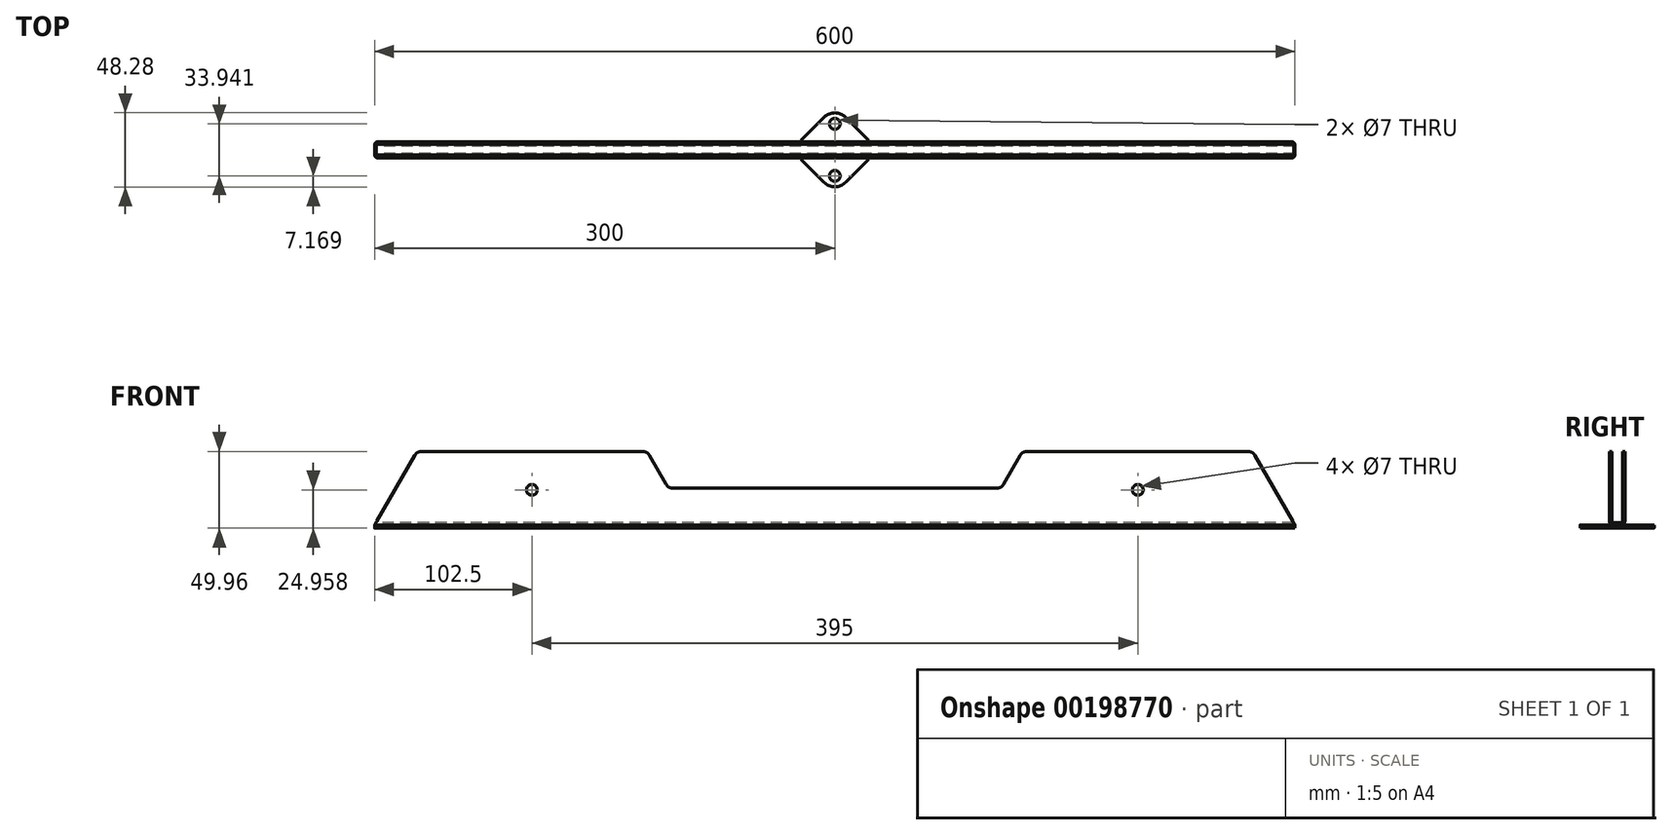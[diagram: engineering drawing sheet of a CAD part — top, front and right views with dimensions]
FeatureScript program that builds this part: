
annotation { "Feature Type Name" : "Feature", "Feature Type Description" : "" }
export const myFeature = defineFeature(function(context is Context, id is Id, definition is map)
    precondition{}
    {
        {
            var Q0;
            Q0=qCreatedBy(makeId("Top.planeOp"),FACE);
            var sketch = newSketch(context, id + "F0", { "sketchPlane" : qUnion([Q0])});
            skLineSegment(sketch, "E0.bottom", {"start": v(-21.21, 7.07) * mm, "end": v(-7.07, 21.21) * mm});
            skLineSegment(sketch, "E0.top", {"start": v(7.07, -21.21) * mm, "end": v(21.21, -7.07) * mm});
            skLineSegment(sketch, "E0.left", {"start": v(-21.21, -7.07) * mm, "end": v(-7.07, -21.21) * mm});
            skLineSegment(sketch, "E0.right", {"start": v(7.07, 21.21) * mm, "end": v(21.21, 7.07) * mm});
            skPoint(sketch, "E0.middle", {"position": v(0, 0) * mm});
            skPoint(sketch, "E1.visualSharp", {"position": v(-28.28, 0) * mm});
            skArc(sketch, "E1.filletArc", {"start": v(-21.21, 7.07) * mm, "mid": v(-24.14, 0) * mm, "end": v(-21.21, -7.07) * mm});
            skPoint(sketch, "E2.visualSharp", {"position": v(0, 28.28) * mm});
            skArc(sketch, "E2.filletArc", {"start": v(7.07, 21.21) * mm, "mid": v(0, 24.14) * mm, "end": v(-7.07, 21.21) * mm});
            skPoint(sketch, "E3.visualSharp", {"position": v(28.28, 0) * mm});
            skArc(sketch, "E3.filletArc", {"start": v(21.21, -7.07) * mm, "mid": v(24.14, 0) * mm, "end": v(21.21, 7.07) * mm});
            skPoint(sketch, "E4.visualSharp", {"position": v(0, -28.28) * mm});
            skArc(sketch, "E4.filletArc", {"start": v(-7.07, -21.21) * mm, "mid": v(0, -24.14) * mm, "end": v(7.07, -21.21) * mm});
            skLineSegment(sketch, "E5.bottom", {"start": v(0, 16.97) * mm, "end": v(-16.97, 0) * mm, "construction": true});
            skLineSegment(sketch, "E5.top", {"start": v(16.97, 0) * mm, "end": v(0, -16.97) * mm, "construction": true});
            skLineSegment(sketch, "E5.left", {"start": v(0, 16.97) * mm, "end": v(16.97, 0) * mm, "construction": true});
            skLineSegment(sketch, "E5.right", {"start": v(-16.97, 0) * mm, "end": v(0, -16.97) * mm, "construction": true});
            skCircle(sketch, "E6", {"center": v(0, 16.97) * mm, "radius": 3.5 * mm});
            skCircle(sketch, "E7", {"center": v(16.97, 0) * mm, "radius": 3.5 * mm});
            skCircle(sketch, "E8", {"center": v(0, -16.97) * mm, "radius": 3.5 * mm});
            skCircle(sketch, "E9", {"center": v(-16.97, 0) * mm, "radius": 3.5 * mm});
            skSolve(sketch);
        }
        {
            var Q0;
            Q0 = qSketchRegion(id + "F0", true);
            extrude(context, id + "F1", {"entities" : qUnion([Q0]), "depth" : 2 * mm});
        }
        {
            var Q0;
            Q0=qCreatedBy(makeId("Front.planeOp"),FACE);
            var sketch = newSketch(context, id + "F2", { "sketchPlane" : qUnion([Q0])});
            skLineSegment(sketch, "E10", {"start": v(0, 2) * mm, "end": v(0, 49.96) * mm, "construction": true});
            skLineSegment(sketch, "E11.bottom", {"start": v(300, 49.96) * mm, "end": v(-300, 49.96) * mm, "construction": true});
            skLineSegment(sketch, "E11.top", {"start": v(300, 2) * mm, "end": v(-300, 2) * mm});
            skLineSegment(sketch, "E11.left", {"start": v(300, 49.96) * mm, "end": v(300, 2) * mm, "construction": true});
            skLineSegment(sketch, "E11.right", {"start": v(-300, 49.96) * mm, "end": v(-300, 2) * mm, "construction": true});
            skPoint(sketch, "E11.middle", {"position": v(0, 25.98) * mm});
            skLineSegment(sketch, "E12", {"start": v(-300, 2) * mm, "end": v(-272.31, 49.96) * mm});
            skLineSegment(sketch, "E13", {"start": v(-272.31, 49.96) * mm, "end": v(-122.31, 49.96) * mm});
            skLineSegment(sketch, "E14", {"start": v(-122.31, 49.96) * mm, "end": v(-108.47, 25.98) * mm});
            skLineSegment(sketch, "E15", {"start": v(-108.47, 25.98) * mm, "end": v(0, 25.98) * mm});
            skLineSegment(sketch, "E16.MirrorCS", {"start": v(122.31, 49.96) * mm, "end": v(108.47, 25.98) * mm});
            skLineSegment(sketch, "E17.MirrorCS", {"start": v(108.47, 25.98) * mm, "end": v(0, 25.98) * mm});
            skLineSegment(sketch, "E18.MirrorCS", {"start": v(272.31, 49.96) * mm, "end": v(122.31, 49.96) * mm});
            skLineSegment(sketch, "E19.MirrorCS", {"start": v(300, 2) * mm, "end": v(272.31, 49.96) * mm});
            skSolve(sketch);
        }
        {
            var Q0;
            Q0 = qSketchRegion(id + "F2", true);
            extrude(context, id + "F3", {"entities" : qUnion([Q0]), "depth" : 10.2 * mm, "symmetric" : true});
        }
        {
            var Q0;
            Q0=makeQuery(id+"F3.opExtrude","CAP_EDGE",EDGE,{"disambiguationData":[OSD([sQuery(id+"F2.wireOp",EDGE,"E11.top")])],"isStart":false});
            var Q1;
            Q1=makeQuery(id+"F3.opExtrude","CAP_EDGE",EDGE,{"disambiguationData":[OSD([sQuery(id+"F2.wireOp",EDGE,"E11.top")])],"isStart":true});
            fillet(context, id + "F4", {"entities" : qUnion([Q0, Q1]), "radius" : 2.6 * mm, "tangentPropagation" : true, "allowEdgeOverflow" : false});
        }
        {
            var Q0;
            Q0=makeQuery(id+"F3.opExtrude","SWEPT_EDGE",EDGE,{"disambiguationData":[OSD([sQuery(id+"F2.wireOp",EDGE,"E12"),sQuery(id+"F2.wireOp",EDGE,"E13")])]});
            var Q1;
            Q1=makeQuery(id+"F3.opExtrude","SWEPT_EDGE",EDGE,{"disambiguationData":[OSD([sQuery(id+"F2.wireOp",EDGE,"E13"),sQuery(id+"F2.wireOp",EDGE,"E14")])]});
            var Q2;
            Q2=makeQuery(id+"F3.opExtrude","SWEPT_EDGE",EDGE,{"disambiguationData":[OSD([sQuery(id+"F2.wireOp",EDGE,"E14"),sQuery(id+"F2.wireOp",EDGE,"E15")])]});
            var Q3;
            Q3=makeQuery(id+"F3.opExtrude","SWEPT_EDGE",EDGE,{"disambiguationData":[OSD([sQuery(id+"F2.wireOp",EDGE,"E16.MirrorCS"),sQuery(id+"F2.wireOp",EDGE,"E18.MirrorCS")])]});
            var Q4;
            Q4=makeQuery(id+"F3.opExtrude","SWEPT_EDGE",EDGE,{"disambiguationData":[OSD([sQuery(id+"F2.wireOp",EDGE,"E16.MirrorCS"),sQuery(id+"F2.wireOp",EDGE,"E17.MirrorCS")])]});
            var Q5;
            Q5=makeQuery(id+"F3.opExtrude","SWEPT_EDGE",EDGE,{"disambiguationData":[OSD([sQuery(id+"F2.wireOp",EDGE,"E18.MirrorCS"),sQuery(id+"F2.wireOp",EDGE,"E19.MirrorCS")])]});
            fillet(context, id + "F5", {"entities" : qUnion([Q0, Q1, Q2, Q3, Q4, Q5]), "radius" : 5 * mm, "tangentPropagation" : true, "allowEdgeOverflow" : false});
        }
        {
            var Q0;
            Q0=makeQuery(id+"F3.opExtrude","SWEPT_FACE",FACE,{"disambiguationData":[OSD([sQuery(id+"F2.wireOp",EDGE,"E12")])]});
            var Q1;
            Q1=makeQuery(id+"F5.opFillet","BLEND_FACE",FACE,{"disambiguationData":[OSD([sQuery(id+"F2.wireOp",EDGE,"E12"),sQuery(id+"F2.wireOp",EDGE,"E13")])]});
            var Q2;
            Q2=makeQuery(id+"F3.opExtrude","SWEPT_FACE",FACE,{"disambiguationData":[OSD([sQuery(id+"F2.wireOp",EDGE,"E13")])]});
            var Q3;
            Q3=makeQuery(id+"F3.opExtrude","SWEPT_FACE",FACE,{"disambiguationData":[OSD([sQuery(id+"F2.wireOp",EDGE,"E15"),sQuery(id+"F2.wireOp",EDGE,"E17.MirrorCS")])]});
            var Q4;
            Q4=makeQuery(id+"F5.opFillet","BLEND_FACE",FACE,{"disambiguationData":[OSD([sQuery(id+"F2.wireOp",EDGE,"E14"),sQuery(id+"F2.wireOp",EDGE,"E15")])]});
            var Q5;
            Q5=makeQuery(id+"F3.opExtrude","SWEPT_FACE",FACE,{"disambiguationData":[OSD([sQuery(id+"F2.wireOp",EDGE,"E14")])]});
            var Q6;
            Q6=makeQuery(id+"F5.opFillet","BLEND_FACE",FACE,{"disambiguationData":[OSD([sQuery(id+"F2.wireOp",EDGE,"E13"),sQuery(id+"F2.wireOp",EDGE,"E14")])]});
            var Q7;
            Q7=makeQuery(id+"F5.opFillet","BLEND_FACE",FACE,{"disambiguationData":[OSD([sQuery(id+"F2.wireOp",EDGE,"E16.MirrorCS"),sQuery(id+"F2.wireOp",EDGE,"E17.MirrorCS")])]});
            var Q8;
            Q8=makeQuery(id+"F3.opExtrude","SWEPT_FACE",FACE,{"disambiguationData":[OSD([sQuery(id+"F2.wireOp",EDGE,"E16.MirrorCS")])]});
            var Q9;
            Q9=makeQuery(id+"F5.opFillet","BLEND_FACE",FACE,{"disambiguationData":[OSD([sQuery(id+"F2.wireOp",EDGE,"E16.MirrorCS"),sQuery(id+"F2.wireOp",EDGE,"E18.MirrorCS")])]});
            var Q10;
            Q10=makeQuery(id+"F3.opExtrude","SWEPT_FACE",FACE,{"disambiguationData":[OSD([sQuery(id+"F2.wireOp",EDGE,"E18.MirrorCS")])]});
            var Q11;
            Q11=makeQuery(id+"F5.opFillet","BLEND_FACE",FACE,{"disambiguationData":[OSD([sQuery(id+"F2.wireOp",EDGE,"E18.MirrorCS"),sQuery(id+"F2.wireOp",EDGE,"E19.MirrorCS")])]});
            var Q12;
            Q12=makeQuery(id+"F3.opExtrude","SWEPT_FACE",FACE,{"disambiguationData":[OSD([sQuery(id+"F2.wireOp",EDGE,"E19.MirrorCS")])]});
            shell(context, id + "F6", {"entities" : qUnion([Q0, Q1, Q2, Q3, Q4, Q5, Q6, Q7, Q8, Q9, Q10, Q11, Q12]), "thickness" : 1.6 * mm});
        }
        {
            var Q0;
            Q0=makeQuery(id+"F1.opExtrude","CAP_FACE",FACE,{"disambiguationData":[OSD([sQuery(id+"F0.wireOp",EDGE,"E0.bottom"),sQuery(id+"F0.wireOp",EDGE,"E0.top"),sQuery(id+"F0.wireOp",EDGE,"E0.left"),sQuery(id+"F0.wireOp",EDGE,"E0.right"),sQuery(id+"F0.wireOp",EDGE,"E1.filletArc"),sQuery(id+"F0.wireOp",EDGE,"E2.filletArc"),sQuery(id+"F0.wireOp",EDGE,"E3.filletArc"),sQuery(id+"F0.wireOp",EDGE,"E4.filletArc"),sQuery(id+"F0.wireOp",EDGE,"E6"),sQuery(id+"F0.wireOp",EDGE,"E7"),sQuery(id+"F0.wireOp",EDGE,"E8"),sQuery(id+"F0.wireOp",EDGE,"E9")])],"isStart":true});
            var sketch = newSketch(context, id + "F7", { "sketchPlane" : qUnion([Q0])});
            skLineSegment(sketch, "E20", {"start": v(-14.14, -14.14) * mm, "end": v(14.14, 14.14) * mm, "construction": true});
            skLineSegment(sketch, "E21.bottom", {"start": v(298, -5.1) * mm, "end": v(-298, -5.1) * mm});
            skLineSegment(sketch, "E21.top", {"start": v(298, 5.1) * mm, "end": v(-298, 5.1) * mm});
            skLineSegment(sketch, "E21.left", {"start": v(300, -3.1) * mm, "end": v(300, 3.1) * mm});
            skLineSegment(sketch, "E21.right", {"start": v(-300, -3.1) * mm, "end": v(-300, 3.1) * mm});
            skPoint(sketch, "E21.middle", {"position": v(0, 0) * mm});
            skPoint(sketch, "E22.visualSharp", {"position": v(300, -5.1) * mm});
            skArc(sketch, "E22.filletArc", {"start": v(298, -5.1) * mm, "mid": v(299.41, -4.51) * mm, "end": v(300, -3.1) * mm});
            skPoint(sketch, "E23.visualSharp", {"position": v(-300, -5.1) * mm});
            skArc(sketch, "E23.filletArc", {"start": v(-300, -3.1) * mm, "mid": v(-299.41, -4.51) * mm, "end": v(-298, -5.1) * mm});
            skPoint(sketch, "E24.visualSharp", {"position": v(300, 5.1) * mm});
            skArc(sketch, "E24.filletArc", {"start": v(300, 3.1) * mm, "mid": v(299.41, 4.51) * mm, "end": v(298, 5.1) * mm});
            skPoint(sketch, "E25.visualSharp", {"position": v(-300, 5.1) * mm});
            skArc(sketch, "E25.filletArc", {"start": v(-298, 5.1) * mm, "mid": v(-299.41, 4.51) * mm, "end": v(-300, 3.1) * mm});
            skSolve(sketch);
        }
        {
            var Q0;
            Q0 = qSketchRegion(id + "F7", true);
            var Q1;
            Q1=makeQuery(id+"F1.opExtrude","CAP_FACE",FACE,{"disambiguationData":[OSD([sQuery(id+"F0.wireOp",EDGE,"E0.bottom"),sQuery(id+"F0.wireOp",EDGE,"E0.top"),sQuery(id+"F0.wireOp",EDGE,"E0.left"),sQuery(id+"F0.wireOp",EDGE,"E0.right"),sQuery(id+"F0.wireOp",EDGE,"E1.filletArc"),sQuery(id+"F0.wireOp",EDGE,"E2.filletArc"),sQuery(id+"F0.wireOp",EDGE,"E3.filletArc"),sQuery(id+"F0.wireOp",EDGE,"E4.filletArc"),sQuery(id+"F0.wireOp",EDGE,"E6"),sQuery(id+"F0.wireOp",EDGE,"E7"),sQuery(id+"F0.wireOp",EDGE,"E8"),sQuery(id+"F0.wireOp",EDGE,"E9")])],"isStart":false});
            extrude(context, id + "F8", {"entities" : qUnion([Q0]), "operationType" : NewBodyOperationType.ADD, "endBound" : BoundingType.UP_TO_SURFACE, "oppositeDirection" : true, "endBoundEntityFace" : qUnion([Q1]), "depth" : 25 * mm});
        }
        {
            var Q0;
            Q0=makeQuery(id+"F3.opExtrude","CAP_FACE",FACE,{"disambiguationData":[OSD([sQuery(id+"F2.wireOp",EDGE,"E11.top"),sQuery(id+"F2.wireOp",EDGE,"E12"),sQuery(id+"F2.wireOp",EDGE,"E13"),sQuery(id+"F2.wireOp",EDGE,"E14"),sQuery(id+"F2.wireOp",EDGE,"E15"),sQuery(id+"F2.wireOp",EDGE,"E16.MirrorCS"),sQuery(id+"F2.wireOp",EDGE,"E17.MirrorCS"),sQuery(id+"F2.wireOp",EDGE,"E18.MirrorCS"),sQuery(id+"F2.wireOp",EDGE,"E19.MirrorCS")])],"isStart":false});
            var sketch = newSketch(context, id + "F9", { "sketchPlane" : qUnion([Q0])});
            skCircle(sketch, "E26", {"center": v(-197.5, 24.96) * mm, "radius": 3.5 * mm});
            skLineSegment(sketch, "E27", {"start": v(0, 0) * mm, "end": v(0, 25.98) * mm, "construction": true});
            skCircle(sketch, "E28.MirrorC", {"center": v(197.5, 24.96) * mm, "radius": 3.5 * mm});
            skSolve(sketch);
        }
        {
            var Q0;
            Q0 = qSketchRegion(id + "F9", true);
            extrude(context, id + "F10", {"entities" : qUnion([Q0]), "operationType" : NewBodyOperationType.REMOVE, "endBound" : BoundingType.THROUGH_ALL, "oppositeDirection" : true, "depth" : 25 * mm});
        }
    });
